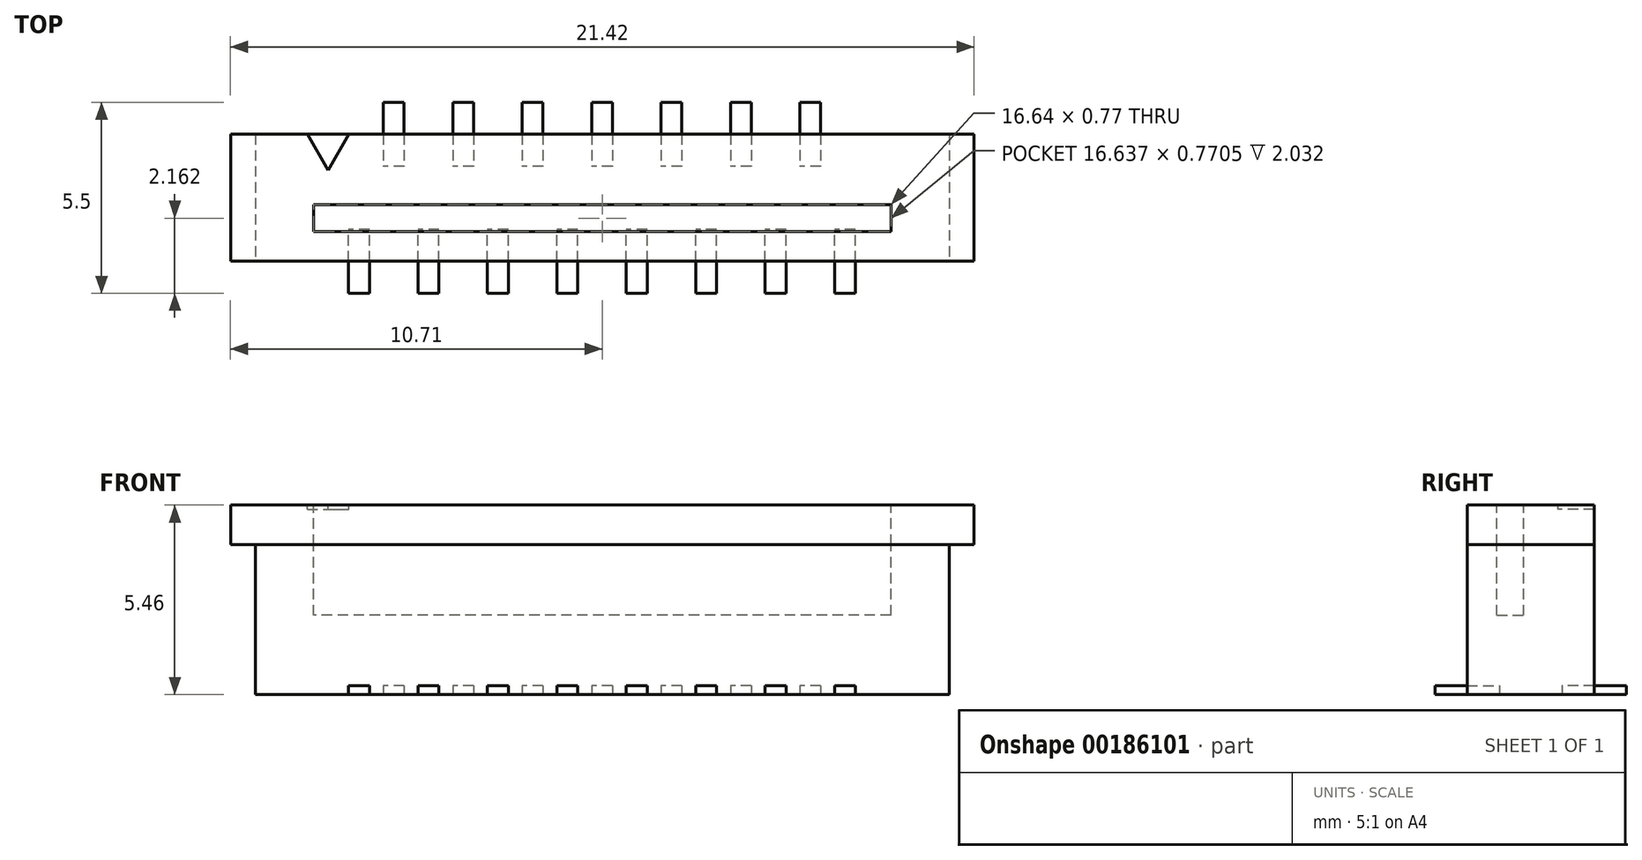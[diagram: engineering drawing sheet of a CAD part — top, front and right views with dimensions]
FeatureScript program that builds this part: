
annotation { "Feature Type Name" : "Feature", "Feature Type Description" : "" }
export const myFeature = defineFeature(function(context is Context, id is Id, definition is map)
    precondition{}
    {
        {
            var Q0;
            Q0=qCreatedBy(makeId("Top.planeOp"),FACE);
            var sketch = newSketch(context, id + "F0", { "sketchPlane" : qUnion([Q0])});
            skLineSegment(sketch, "E0.bottom", {"start": v(10, 1.83) * mm, "end": v(-10, 1.83) * mm});
            skLineSegment(sketch, "E0.top", {"start": v(10, -1.83) * mm, "end": v(-10, -1.83) * mm});
            skLineSegment(sketch, "E0.left", {"start": v(10, 1.83) * mm, "end": v(10, -1.83) * mm});
            skLineSegment(sketch, "E0.right", {"start": v(-10, 1.83) * mm, "end": v(-10, -1.83) * mm});
            skPoint(sketch, "E0.middle", {"position": v(0, 0) * mm});
            skSolve(sketch);
        }
        {
            var Q0;
            Q0 = qSketchRegion(id + "F0", true);
            extrude(context, id + "F1", {"entities" : qUnion([Q0]), "depth" : 4.32 * mm});
        }
        {
            var Q0;
            Q0=makeQuery(id+"F1.opExtrude","CAP_FACE",FACE,{"disambiguationData":[OSD([sQuery(id+"F0.wireOp",EDGE,"E0.bottom"),sQuery(id+"F0.wireOp",EDGE,"E0.top"),sQuery(id+"F0.wireOp",EDGE,"E0.left"),sQuery(id+"F0.wireOp",EDGE,"E0.right")])],"isStart":false});
            var sketch = newSketch(context, id + "F2", { "sketchPlane" : qUnion([Q0])});
            skLineSegment(sketch, "E1.bottom", {"start": v(-10.7, 1.83) * mm, "end": v(10.7, 1.83) * mm});
            skLineSegment(sketch, "E1.top", {"start": v(-10.7, -1.83) * mm, "end": v(10.7, -1.83) * mm});
            skLineSegment(sketch, "E1.left", {"start": v(-10.7, 1.83) * mm, "end": v(-10.7, -1.83) * mm});
            skLineSegment(sketch, "E1.right", {"start": v(10.7, 1.83) * mm, "end": v(10.7, -1.83) * mm});
            skPoint(sketch, "E1.middle", {"position": v(0, 0) * mm});
            skSolve(sketch);
        }
        {
            var Q0;
            Q0 = qSketchRegion(id + "F2", true);
            extrude(context, id + "F3", {"entities" : qUnion([Q0]), "depth" : 1.14 * mm});
        }
        {
            var Q0;
            Q0=makeQuery(id+"F1.opExtrude","CAP_FACE",FACE,{"disambiguationData":[OSD([sQuery(id+"F0.wireOp",EDGE,"E0.bottom"),sQuery(id+"F0.wireOp",EDGE,"E0.top"),sQuery(id+"F0.wireOp",EDGE,"E0.left"),sQuery(id+"F0.wireOp",EDGE,"E0.right")])],"isStart":true});
            var sketch = newSketch(context, id + "F4", { "sketchPlane" : qUnion([Q0])});
            skLineSegment(sketch, "E2.bottom", {"start": v(-6.7, 2.75) * mm, "end": v(-7.3, 2.75) * mm});
            skLineSegment(sketch, "E2.top", {"start": v(-6.7, 0.9) * mm, "end": v(-7.3, 0.9) * mm});
            skLineSegment(sketch, "E2.left", {"start": v(-6.7, 2.75) * mm, "end": v(-6.7, 0.9) * mm});
            skLineSegment(sketch, "E2.right", {"start": v(-7.3, 2.75) * mm, "end": v(-7.3, 0.9) * mm});
            skPoint(sketch, "E2.middle", {"position": v(-7, 1.83) * mm});
            skLineSegment(sketch, "E3.1.0.0", {"start": v(-4.7, 2.75) * mm, "end": v(-4.7, 0.9) * mm});
            skLineSegment(sketch, "E3.1.0.1", {"start": v(-4.7, 2.75) * mm, "end": v(-5.3, 2.75) * mm});
            skLineSegment(sketch, "E3.1.0.2", {"start": v(-5.3, 2.75) * mm, "end": v(-5.3, 0.9) * mm});
            skLineSegment(sketch, "E3.1.0.3", {"start": v(-4.7, 0.9) * mm, "end": v(-5.3, 0.9) * mm});
            skLineSegment(sketch, "E3.2.0.0", {"start": v(-2.7, 2.75) * mm, "end": v(-2.7, 0.9) * mm});
            skLineSegment(sketch, "E3.2.0.1", {"start": v(-2.7, 2.75) * mm, "end": v(-3.3, 2.75) * mm});
            skLineSegment(sketch, "E3.2.0.2", {"start": v(-3.3, 2.75) * mm, "end": v(-3.3, 0.9) * mm});
            skLineSegment(sketch, "E3.2.0.3", {"start": v(-2.7, 0.9) * mm, "end": v(-3.3, 0.9) * mm});
            skLineSegment(sketch, "E3.3.0.0", {"start": v(-0.7, 2.75) * mm, "end": v(-0.7, 0.9) * mm});
            skLineSegment(sketch, "E3.3.0.1", {"start": v(-0.7, 2.75) * mm, "end": v(-1.3, 2.75) * mm});
            skLineSegment(sketch, "E3.3.0.2", {"start": v(-1.3, 2.75) * mm, "end": v(-1.3, 0.9) * mm});
            skLineSegment(sketch, "E3.3.0.3", {"start": v(-0.7, 0.9) * mm, "end": v(-1.3, 0.9) * mm});
            skLineSegment(sketch, "E3.4.0.0", {"start": v(1.3, 2.75) * mm, "end": v(1.3, 0.9) * mm});
            skLineSegment(sketch, "E3.4.0.1", {"start": v(1.3, 2.75) * mm, "end": v(0.7, 2.75) * mm});
            skLineSegment(sketch, "E3.4.0.2", {"start": v(0.7, 2.75) * mm, "end": v(0.7, 0.9) * mm});
            skLineSegment(sketch, "E3.4.0.3", {"start": v(1.3, 0.9) * mm, "end": v(0.7, 0.9) * mm});
            skLineSegment(sketch, "E3.5.0.0", {"start": v(3.3, 2.75) * mm, "end": v(3.3, 0.9) * mm});
            skLineSegment(sketch, "E3.5.0.1", {"start": v(3.3, 2.75) * mm, "end": v(2.7, 2.75) * mm});
            skLineSegment(sketch, "E3.5.0.2", {"start": v(2.7, 2.75) * mm, "end": v(2.7, 0.9) * mm});
            skLineSegment(sketch, "E3.5.0.3", {"start": v(3.3, 0.9) * mm, "end": v(2.7, 0.9) * mm});
            skLineSegment(sketch, "E3.6.0.0", {"start": v(5.3, 2.75) * mm, "end": v(5.3, 0.9) * mm});
            skLineSegment(sketch, "E3.6.0.1", {"start": v(5.3, 2.75) * mm, "end": v(4.7, 2.75) * mm});
            skLineSegment(sketch, "E3.6.0.2", {"start": v(4.7, 2.75) * mm, "end": v(4.7, 0.9) * mm});
            skLineSegment(sketch, "E3.6.0.3", {"start": v(5.3, 0.9) * mm, "end": v(4.7, 0.9) * mm});
            skLineSegment(sketch, "E3.7.0.0", {"start": v(7.3, 2.75) * mm, "end": v(7.3, 0.9) * mm});
            skLineSegment(sketch, "E3.7.0.1", {"start": v(7.3, 2.75) * mm, "end": v(6.7, 2.75) * mm});
            skLineSegment(sketch, "E3.7.0.2", {"start": v(6.7, 2.75) * mm, "end": v(6.7, 0.9) * mm});
            skLineSegment(sketch, "E3.7.0.3", {"start": v(7.3, 0.9) * mm, "end": v(6.7, 0.9) * mm});
            skLineSegment(sketch, "E3.direction1", {"start": v(-6.7, 0.9) * mm, "end": v(-4.7, 0.9) * mm, "construction": true});
            skLineSegment(sketch, "E4.bottom", {"start": v(-5.7, -2.75) * mm, "end": v(-6.3, -2.75) * mm});
            skLineSegment(sketch, "E4.top", {"start": v(-5.7, -0.9) * mm, "end": v(-6.3, -0.9) * mm});
            skLineSegment(sketch, "E4.left", {"start": v(-5.7, -2.75) * mm, "end": v(-5.7, -0.9) * mm});
            skLineSegment(sketch, "E4.right", {"start": v(-6.3, -2.75) * mm, "end": v(-6.3, -0.9) * mm});
            skPoint(sketch, "E4.middle", {"position": v(-6, -1.83) * mm});
            skLineSegment(sketch, "E5.1.0.0", {"start": v(-3.7, -2.75) * mm, "end": v(-3.7, -0.9) * mm});
            skLineSegment(sketch, "E5.1.0.1", {"start": v(-3.7, -2.75) * mm, "end": v(-4.3, -2.75) * mm});
            skLineSegment(sketch, "E5.1.0.2", {"start": v(-4.3, -2.75) * mm, "end": v(-4.3, -0.9) * mm});
            skLineSegment(sketch, "E5.1.0.3", {"start": v(-3.7, -0.9) * mm, "end": v(-4.3, -0.9) * mm});
            skLineSegment(sketch, "E5.2.0.0", {"start": v(-1.7, -2.75) * mm, "end": v(-1.7, -0.9) * mm});
            skLineSegment(sketch, "E5.2.0.1", {"start": v(-1.7, -2.75) * mm, "end": v(-2.3, -2.75) * mm});
            skLineSegment(sketch, "E5.2.0.2", {"start": v(-2.3, -2.75) * mm, "end": v(-2.3, -0.9) * mm});
            skLineSegment(sketch, "E5.2.0.3", {"start": v(-1.7, -0.9) * mm, "end": v(-2.3, -0.9) * mm});
            skLineSegment(sketch, "E5.3.0.0", {"start": v(0.3, -2.75) * mm, "end": v(0.3, -0.9) * mm});
            skLineSegment(sketch, "E5.3.0.1", {"start": v(0.3, -2.75) * mm, "end": v(-0.3, -2.75) * mm});
            skLineSegment(sketch, "E5.3.0.2", {"start": v(-0.3, -2.75) * mm, "end": v(-0.3, -0.9) * mm});
            skLineSegment(sketch, "E5.3.0.3", {"start": v(0.3, -0.9) * mm, "end": v(-0.3, -0.9) * mm});
            skLineSegment(sketch, "E5.4.0.0", {"start": v(2.3, -2.75) * mm, "end": v(2.3, -0.9) * mm});
            skLineSegment(sketch, "E5.4.0.1", {"start": v(2.3, -2.75) * mm, "end": v(1.7, -2.75) * mm});
            skLineSegment(sketch, "E5.4.0.2", {"start": v(1.7, -2.75) * mm, "end": v(1.7, -0.9) * mm});
            skLineSegment(sketch, "E5.4.0.3", {"start": v(2.3, -0.9) * mm, "end": v(1.7, -0.9) * mm});
            skLineSegment(sketch, "E5.5.0.0", {"start": v(4.3, -2.75) * mm, "end": v(4.3, -0.9) * mm});
            skLineSegment(sketch, "E5.5.0.1", {"start": v(4.3, -2.75) * mm, "end": v(3.7, -2.75) * mm});
            skLineSegment(sketch, "E5.5.0.2", {"start": v(3.7, -2.75) * mm, "end": v(3.7, -0.9) * mm});
            skLineSegment(sketch, "E5.5.0.3", {"start": v(4.3, -0.9) * mm, "end": v(3.7, -0.9) * mm});
            skLineSegment(sketch, "E5.6.0.0", {"start": v(6.3, -2.75) * mm, "end": v(6.3, -0.9) * mm});
            skLineSegment(sketch, "E5.6.0.1", {"start": v(6.3, -2.75) * mm, "end": v(5.7, -2.75) * mm});
            skLineSegment(sketch, "E5.6.0.2", {"start": v(5.7, -2.75) * mm, "end": v(5.7, -0.9) * mm});
            skLineSegment(sketch, "E5.6.0.3", {"start": v(6.3, -0.9) * mm, "end": v(5.7, -0.9) * mm});
            skLineSegment(sketch, "E5.direction1", {"start": v(-6.3, -2.75) * mm, "end": v(-4.3, -2.75) * mm, "construction": true});
            skSolve(sketch);
        }
        {
            var Q0;
            Q0 = qSketchRegion(id + "F4", true);
            extrude(context, id + "F5", {"entities" : qUnion([Q0]), "oppositeDirection" : true, "depth" : 0.25 * mm});
        }
        {
            var Q0;
            Q0=makeQuery(id+"F3.opExtrude","CAP_FACE",FACE,{"disambiguationData":[OSD([sQuery(id+"F2.wireOp",EDGE,"E1.bottom"),sQuery(id+"F2.wireOp",EDGE,"E1.top"),sQuery(id+"F2.wireOp",EDGE,"E1.left"),sQuery(id+"F2.wireOp",EDGE,"E1.right")])],"isStart":false});
            var sketch = newSketch(context, id + "F6", { "sketchPlane" : qUnion([Q0])});
            skLineSegment(sketch, "E6.bottom", {"start": v(8.32, -0.97) * mm, "end": v(-8.32, -0.97) * mm});
            skLineSegment(sketch, "E6.top", {"start": v(8.32, -0.2) * mm, "end": v(-8.32, -0.2) * mm});
            skLineSegment(sketch, "E6.left", {"start": v(8.32, -0.97) * mm, "end": v(8.32, -0.2) * mm});
            skLineSegment(sketch, "E6.right", {"start": v(-8.32, -0.97) * mm, "end": v(-8.32, -0.2) * mm});
            skLineSegment(sketch, "E7", {"start": v(0, -0.2) * mm, "end": v(0, 1.83) * mm, "construction": true});
            skSolve(sketch);
        }
        {
            var Q0;
            Q0 = qSketchRegion(id + "F6", true);
            extrude(context, id + "F7", {"entities" : qUnion([Q0]), "operationType" : NewBodyOperationType.REMOVE, "oppositeDirection" : true, "depth" : 3.17 * mm});
        }
        {
            var Q0;
            Q0=makeQuery(id+"F3.opExtrude","CAP_FACE",FACE,{"disambiguationData":[OSD([sQuery(id+"F2.wireOp",EDGE,"E1.bottom"),sQuery(id+"F2.wireOp",EDGE,"E1.top"),sQuery(id+"F2.wireOp",EDGE,"E1.left"),sQuery(id+"F2.wireOp",EDGE,"E1.right")])],"isStart":false});
            var sketch = newSketch(context, id + "F8", { "sketchPlane" : qUnion([Q0])});
            skLineSegment(sketch, "E8", {"start": v(-7.3, 1.83) * mm, "end": v(-8.5, 1.83) * mm});
            skLineSegment(sketch, "E9", {"start": v(-8.5, 1.83) * mm, "end": v(-7.9, 0.79) * mm});
            skLineSegment(sketch, "E10", {"start": v(-7.9, 0.79) * mm, "end": v(-7.3, 1.83) * mm});
            skSolve(sketch);
        }
        {
            var Q0;
            Q0 = qSketchRegion(id + "F8", true);
            extrude(context, id + "F9", {"entities" : qUnion([Q0]), "operationType" : NewBodyOperationType.REMOVE, "oppositeDirection" : true, "depth" : 0.13 * mm});
        }
    });
